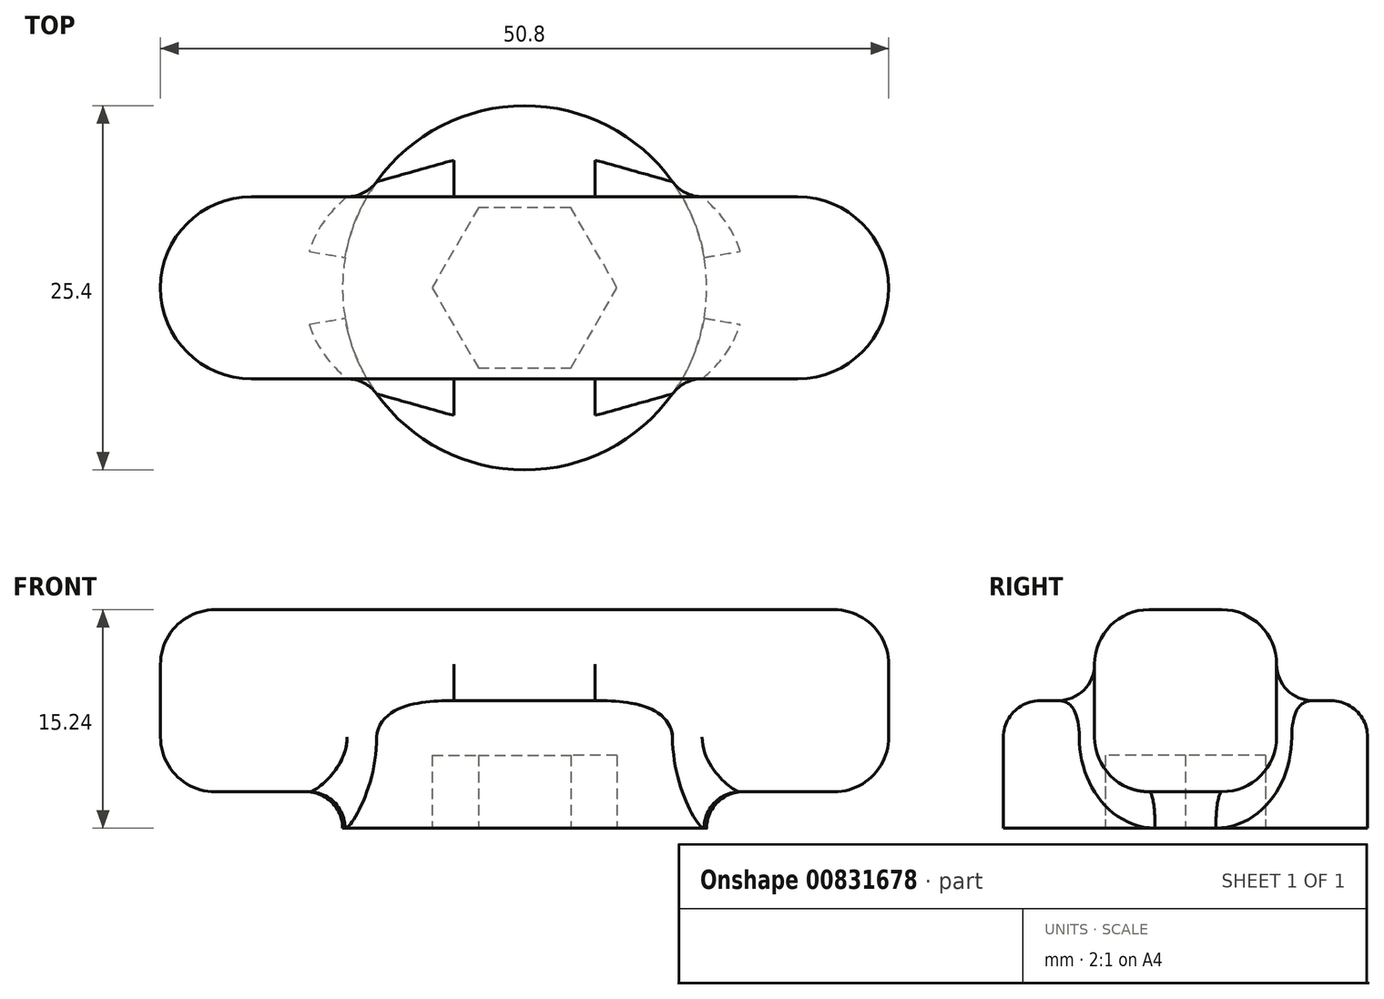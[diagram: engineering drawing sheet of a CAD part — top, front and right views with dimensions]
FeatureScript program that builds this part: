
annotation { "Feature Type Name" : "Feature", "Feature Type Description" : "" }
export const myFeature = defineFeature(function(context is Context, id is Id, definition is map)
    precondition{}
    {
        {
            var Q0;
            Q0=qCreatedBy(makeId("Top.planeOp"),FACE);
            var sketch = newSketch(context, id + "F0", { "sketchPlane" : qUnion([Q0])});
            skCircle(sketch, "E0", {"center": v(0, 0) * mm, "radius": 12.7 * mm});
            skSolve(sketch);
        }
        {
            var Q0;
            Q0=makeQuery(id+"F0.imprint","IMPRINT",FACE,{"disambiguationData":[TD([[makeQuery(id+"F0.imprint","IMPRINT",EDGE,{"derivedFrom":sQuery(id+"F0.wireOp",EDGE,"E0")}),1.0]])]});
            extrude(context, id + "F1", {"entities" : qUnion([Q0]), "depth" : 8.9 * mm, "offsetDistance" : 25.4 * mm});
        }
        {
            var Q0;
            Q0=makeQuery(id+"F1.opExtrude","CAP_FACE",FACE,{"disambiguationData":[OSD([sQuery(id+"F0.wireOp",EDGE,"E0")])],"isStart":false});
            var sketch = newSketch(context, id + "F2", { "sketchPlane" : qUnion([Q0])});
            skLineSegment(sketch, "E1.bottom", {"start": v(-25.4, 6.35) * mm, "end": v(25.4, 6.35) * mm});
            skLineSegment(sketch, "E1.top", {"start": v(-25.4, -6.35) * mm, "end": v(25.4, -6.35) * mm});
            skLineSegment(sketch, "E1.left", {"start": v(-25.4, 6.35) * mm, "end": v(-25.4, -6.35) * mm});
            skLineSegment(sketch, "E1.right", {"start": v(25.4, 6.35) * mm, "end": v(25.4, -6.35) * mm});
            skPoint(sketch, "E1.middle", {"position": v(0, 0) * mm});
            skSolve(sketch);
        }
        {
            var Q0;
            {var subQ0=sQuery(id+"F2.wireOp",EDGE,"E1.left");Q0=makeQuery(id+"F2.imprint","IMPRINT",FACE,{"disambiguationData":[TD([[makeQuery(id+"F2.imprint","IMPRINT",EDGE,{"derivedFrom":subQ0}),1.0]])]});}
            var Q1;
            {var subQ0=sQuery(id+"F2.wireOp",EDGE,"E1.bottom");var subQ1=makeQuery(id+"F1.opExtrude","CAP_EDGE",EDGE,{"disambiguationData":[OSD([sQuery(id+"F0.wireOp",EDGE,"E0")])],"isStart":false});var subQ2=makeQuery(id+"F2.imprint","INTERSECT",VERTEX,{"disambiguationData":[OD(0.0)],"derivedFrom":[subQ1,subQ0]});Q1=makeQuery(id+"F2.imprint","IMPRINT",FACE,{"disambiguationData":[TD([[makeQuery(id+"F2.imprint","IMPRINT",EDGE,{"disambiguationData":[TD([[subQ2,-1.0]])],"derivedFrom":subQ0}),-1.0]])]});}
            var Q2;
            {var subQ0=sQuery(id+"F2.wireOp",EDGE,"E1.right");Q2=makeQuery(id+"F2.imprint","IMPRINT",FACE,{"disambiguationData":[TD([[makeQuery(id+"F2.imprint","IMPRINT",EDGE,{"derivedFrom":subQ0}),-1.0]])]});}
            extrude(context, id + "F3", {"entities" : qUnion([Q0, Q1, Q2]), "operationType" : NewBodyOperationType.ADD, "depth" : 6.35 * mm, "offsetDistance" : 25.4 * mm, "hasSecondDirection" : true, "secondDirectionOppositeDirection" : true, "secondDirectionDepth" : 6.35 * mm});
        }
        {
            var Q0;
            Q0=makeQuery(id+"F1.opExtrude","CAP_FACE",FACE,{"disambiguationData":[OSD([sQuery(id+"F0.wireOp",EDGE,"E0")])],"isStart":true});
            var sketch = newSketch(context, id + "F4", { "sketchPlane" : qUnion([Q0])});
            skCircle(sketch, "E2.cCircle", {"center": v(0, 0) * mm, "radius": 5.59 * mm, "construction": true});
            skLineSegment(sketch, "E2.0", {"start": v(-3.23, 5.59) * mm, "end": v(3.23, 5.59) * mm});
            skLineSegment(sketch, "E2.1", {"start": v(3.23, 5.59) * mm, "end": v(6.45, 0) * mm});
            skLineSegment(sketch, "E2.2", {"start": v(6.45, 0) * mm, "end": v(3.23, -5.59) * mm});
            skLineSegment(sketch, "E2.3", {"start": v(3.23, -5.59) * mm, "end": v(-3.23, -5.59) * mm});
            skLineSegment(sketch, "E2.4", {"start": v(-3.23, -5.59) * mm, "end": v(-6.45, 0) * mm});
            skLineSegment(sketch, "E2.5", {"start": v(-6.45, 0) * mm, "end": v(-3.23, 5.59) * mm});
            skPoint(sketch, "E2.0.midPoint", {"position": v(0, 5.59) * mm});
            skSolve(sketch);
        }
        {
            var Q0;
            Q0=makeQuery(id+"F4.imprint","IMPRINT",FACE,{"disambiguationData":[TD([[makeQuery(id+"F4.imprint","IMPRINT",EDGE,{"derivedFrom":sQuery(id+"F4.wireOp",EDGE,"E2.0")}),-1.0]])]});
            extrude(context, id + "F5", {"entities" : qUnion([Q0]), "operationType" : NewBodyOperationType.REMOVE, "oppositeDirection" : true, "depth" : 5.08 * mm, "offsetDistance" : 25.4 * mm});
        }
        {
            var Q0;
            Q0=makeQuery(id+"F3.opExtrude","SWEPT_EDGE",EDGE,{"disambiguationData":[OSD([sQuery(id+"F2.wireOp",EDGE,"E1.bottom"),sQuery(id+"F2.wireOp",EDGE,"E1.right")])]});
            var Q1;
            Q1=makeQuery(id+"F3.opExtrude","SWEPT_EDGE",EDGE,{"disambiguationData":[OSD([sQuery(id+"F2.wireOp",EDGE,"E1.top"),sQuery(id+"F2.wireOp",EDGE,"E1.right")])]});
            var Q2;
            Q2=makeQuery(id+"F3.opExtrude","SWEPT_EDGE",EDGE,{"disambiguationData":[OSD([sQuery(id+"F2.wireOp",EDGE,"E1.bottom"),sQuery(id+"F2.wireOp",EDGE,"E1.left")])]});
            var Q3;
            Q3=makeQuery(id+"F3.opExtrude","SWEPT_EDGE",EDGE,{"disambiguationData":[OSD([sQuery(id+"F2.wireOp",EDGE,"E1.top"),sQuery(id+"F2.wireOp",EDGE,"E1.left")])]});
            fillet(context, id + "F6", {"entities" : qUnion([Q0, Q1, Q2, Q3]), "radius" : 6.35 * mm, "tangentPropagation" : true, "allowEdgeOverflow" : false});
        }
        {
            var Q0;
            Q0=makeQuery(id+"F3.opExtrude","CAP_EDGE",EDGE,{"disambiguationData":[OSD([sQuery(id+"F2.wireOp",EDGE,"E1.bottom")])],"isStart":false});
            var Q1;
            {var subQ0=sQuery(id+"F2.wireOp",EDGE,"E1.bottom");var subQ1=sQuery(id+"F2.wireOp",EDGE,"E1.right");Q1=makeQuery(id+"F3.boolean.opBoolean","SPLIT",EDGE,{"disambiguationData":[TD([makeQuery(id+"F3.opExtrude","SWEPT_FACE",FACE,{"disambiguationData":[OSD([subQ1])]})])],"derivedFrom":makeQuery(id+"F3.opExtrude","CAP_EDGE",EDGE,{"disambiguationData":[OSD([subQ0])],"isStart":true})});}
            var Q2;
            {var subQ0=sQuery(id+"F2.wireOp",EDGE,"E1.bottom");var subQ1=sQuery(id+"F2.wireOp",EDGE,"E1.left");Q2=makeQuery(id+"F3.boolean.opBoolean","SPLIT",EDGE,{"disambiguationData":[TD([makeQuery(id+"F3.opExtrude","SWEPT_FACE",FACE,{"disambiguationData":[OSD([subQ1])]})])],"derivedFrom":makeQuery(id+"F3.opExtrude","CAP_EDGE",EDGE,{"disambiguationData":[OSD([subQ0])],"isStart":true})});}
            fillet(context, id + "F7", {"entities" : qUnion([Q0, Q1, Q2]), "radius" : 3.8 * mm, "tangentPropagation" : true, "allowEdgeOverflow" : false});
        }
        {
            var Q0;
            Q0=makeQuery(id+"F3.boolean.opBoolean","INTERSECT",EDGE,{"derivedFrom":[makeQuery(id+"F1.opExtrude","CAP_FACE",FACE,{"disambiguationData":[OSD([sQuery(id+"F0.wireOp",EDGE,"E0")])],"isStart":false}),makeQuery(id+"F3.opExtrude","SWEPT_FACE",FACE,{"disambiguationData":[OSD([sQuery(id+"F2.wireOp",EDGE,"E1.top")])]})]});
            var Q1;
            Q1=makeQuery(id+"F3.boolean.opBoolean","INTERSECT",EDGE,{"derivedFrom":[makeQuery(id+"F1.opExtrude","CAP_FACE",FACE,{"disambiguationData":[OSD([sQuery(id+"F0.wireOp",EDGE,"E0")])],"isStart":false}),makeQuery(id+"F3.opExtrude","SWEPT_FACE",FACE,{"disambiguationData":[OSD([sQuery(id+"F2.wireOp",EDGE,"E1.bottom")])]})]});
            var Q2;
            {var subQ0=makeQuery(id+"F1.opExtrude","SWEPT_FACE",FACE,{"disambiguationData":[OSD([sQuery(id+"F0.wireOp",EDGE,"E0")])]});var subQ1=sQuery(id+"F2.wireOp",EDGE,"E1.bottom");var subQ2=sQuery(id+"F2.wireOp",EDGE,"E1.left");Q2=makeQuery(id+"F7.opFillet","BLEND_EDGE",EDGE,{"blendedFrom":[makeQuery(id+"F3.boolean.opBoolean","SPLIT",EDGE,{"disambiguationData":[TD([makeQuery(id+"F3.opExtrude","SWEPT_FACE",FACE,{"disambiguationData":[OSD([subQ2])]})])],"derivedFrom":makeQuery(id+"F3.opExtrude","CAP_EDGE",EDGE,{"disambiguationData":[OSD([subQ1])],"isStart":true})}),subQ0],"blendedInto":[subQ0]});}
            var Q3;
            {var subQ0=makeQuery(id+"F1.opExtrude","SWEPT_FACE",FACE,{"disambiguationData":[OSD([sQuery(id+"F0.wireOp",EDGE,"E0")])]});var subQ1=sQuery(id+"F2.wireOp",EDGE,"E1.top");var subQ2=sQuery(id+"F2.wireOp",EDGE,"E1.right");Q3=makeQuery(id+"F7.opFillet","BLEND_EDGE",EDGE,{"blendedFrom":[makeQuery(id+"F3.boolean.opBoolean","SPLIT",EDGE,{"disambiguationData":[TD([makeQuery(id+"F3.opExtrude","SWEPT_FACE",FACE,{"disambiguationData":[OSD([subQ2])]})])],"derivedFrom":makeQuery(id+"F3.opExtrude","CAP_EDGE",EDGE,{"disambiguationData":[OSD([subQ1])],"isStart":true})}),subQ0],"blendedInto":[subQ0]});}
            var Q4;
            {var subQ0=sQuery(id+"F0.wireOp",EDGE,"E0");Q4=makeQuery(id+"F3.boolean.opBoolean","SPLIT",EDGE,{"disambiguationData":[TD([makeQuery(id+"F3.opExtrude","SWEPT_FACE",FACE,{"disambiguationData":[OSD([sQuery(id+"F2.wireOp",EDGE,"E1.bottom")])]})])],"derivedFrom":makeQuery(id+"F1.opExtrude","CAP_EDGE",EDGE,{"disambiguationData":[OSD([subQ0])],"isStart":false})});}
            var Q5;
            {var subQ0=sQuery(id+"F0.wireOp",EDGE,"E0");Q5=makeQuery(id+"F3.boolean.opBoolean","SPLIT",EDGE,{"disambiguationData":[TD([makeQuery(id+"F3.opExtrude","SWEPT_FACE",FACE,{"disambiguationData":[OSD([sQuery(id+"F2.wireOp",EDGE,"E1.top")])]})])],"derivedFrom":makeQuery(id+"F1.opExtrude","CAP_EDGE",EDGE,{"disambiguationData":[OSD([subQ0])],"isStart":false})});}
            fillet(context, id + "F8", {"entities" : qUnion([Q0, Q1, Q2, Q3, Q4, Q5]), "radius" : 2.54 * mm, "tangentPropagation" : true, "allowEdgeOverflow" : false});
        }
    });
